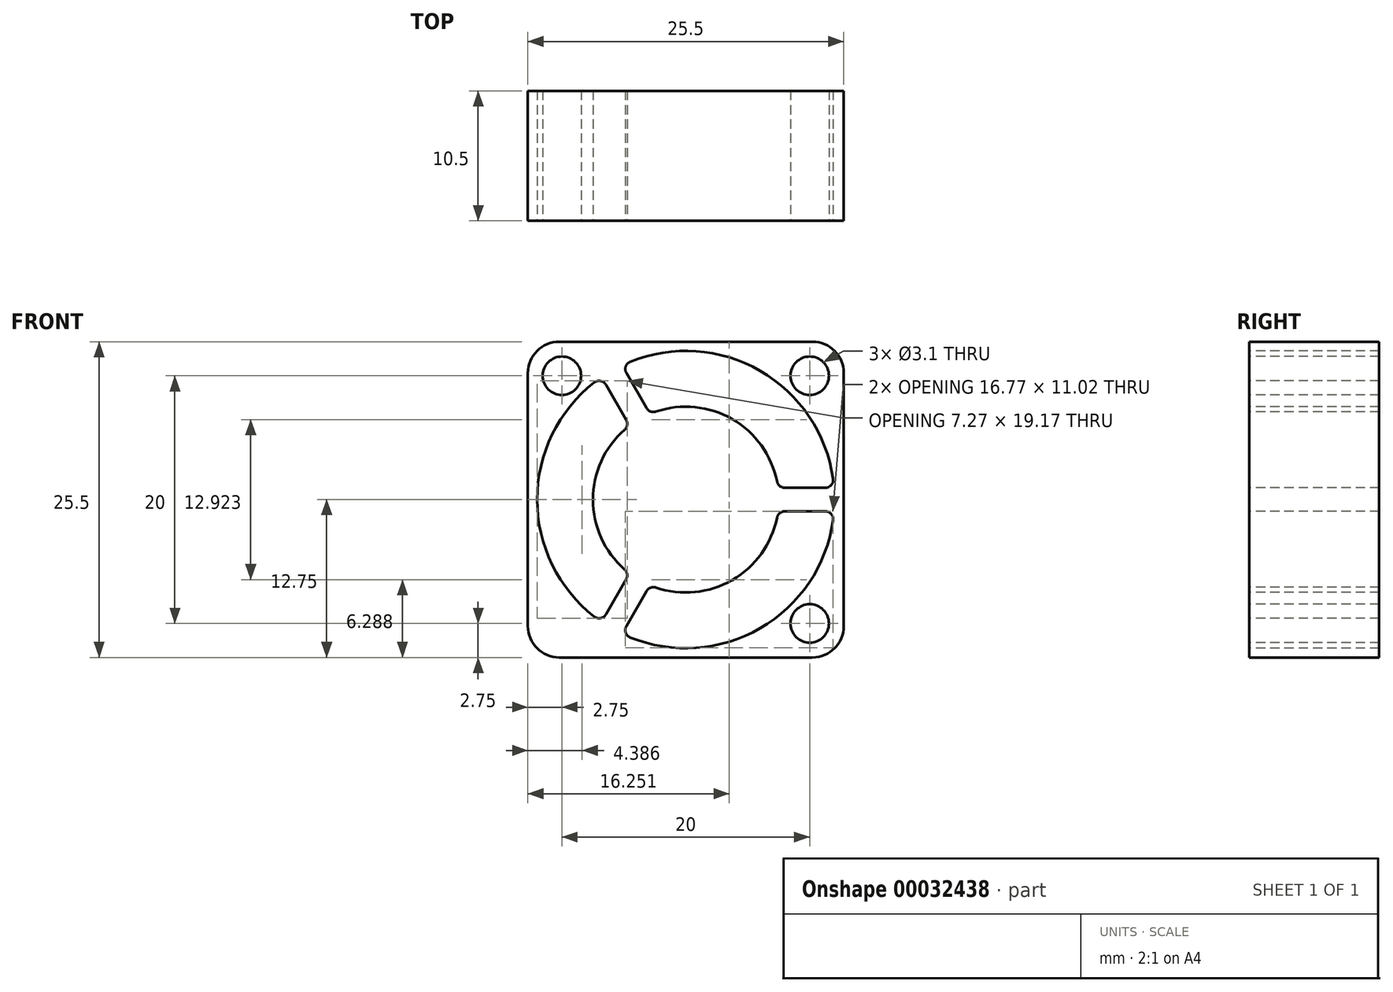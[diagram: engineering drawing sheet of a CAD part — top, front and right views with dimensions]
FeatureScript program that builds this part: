
annotation { "Feature Type Name" : "Feature", "Feature Type Description" : "" }
export const myFeature = defineFeature(function(context is Context, id is Id, definition is map)
    precondition{}
    {
        {
            var Q0;
            Q0=qCreatedBy(makeId("Front.planeOp"),FACE);
            var sketch = newSketch(context, id + "F0", { "sketchPlane" : qUnion([Q0])});
            skLineSegment(sketch, "E0.rect.bottom", {"start": v(12.75, 12.75) * mm, "end": v(-12.75, 12.75) * mm});
            skLineSegment(sketch, "E0.rect.top", {"start": v(12.75, -12.75) * mm, "end": v(-12.75, -12.75) * mm});
            skLineSegment(sketch, "E0.rect.left", {"start": v(12.75, 12.75) * mm, "end": v(12.75, -12.75) * mm});
            skLineSegment(sketch, "E0.rect.right", {"start": v(-12.75, 12.75) * mm, "end": v(-12.75, -12.75) * mm});
            skPoint(sketch, "E0.rect.middle", {"position": v(0, 0) * mm});
            skSolve(sketch);
        }
        {
            var Q0;
            Q0=makeQuery(id+"F0.imprint","IMPRINT",FACE,{"disambiguationData":[TD([[makeQuery(id+"F0.imprint","IMPRINT",EDGE,{"derivedFrom":sQuery(id+"F0.wireOp",EDGE,"E0.rect.bottom")}),1.0]])]});
            extrude(context, id + "F1", {"entities" : qUnion([Q0]), "depth" : 10.5 * mm});
        }
        {
            var Q0;
            Q0=makeQuery(id+"F1.opExtrude","SWEPT_EDGE",EDGE,{"disambiguationData":[OSD([sQuery(id+"F0.wireOp",EDGE,"E0.rect.bottom"),sQuery(id+"F0.wireOp",EDGE,"E0.rect.left")])]});
            var Q1;
            Q1=makeQuery(id+"F1.opExtrude","SWEPT_EDGE",EDGE,{"disambiguationData":[OSD([sQuery(id+"F0.wireOp",EDGE,"E0.rect.bottom"),sQuery(id+"F0.wireOp",EDGE,"E0.rect.right")])]});
            var Q2;
            Q2=makeQuery(id+"F1.opExtrude","SWEPT_EDGE",EDGE,{"disambiguationData":[OSD([sQuery(id+"F0.wireOp",EDGE,"E0.rect.top"),sQuery(id+"F0.wireOp",EDGE,"E0.rect.left")])]});
            var Q3;
            Q3=makeQuery(id+"F1.opExtrude","SWEPT_EDGE",EDGE,{"disambiguationData":[OSD([sQuery(id+"F0.wireOp",EDGE,"E0.rect.top"),sQuery(id+"F0.wireOp",EDGE,"E0.rect.right")])]});
            fillet(context, id + "F2", {"entities" : qUnion([Q0, Q1, Q2, Q3]), "radius" : 2.54 * mm, "tangentPropagation" : true, "allowEdgeOverflow" : false});
        }
        {
            var Q0;
            Q0=makeQuery(id+"F1.opExtrude","CAP_FACE",FACE,{"disambiguationData":[OSD([sQuery(id+"F0.wireOp",EDGE,"E0.rect.bottom"),sQuery(id+"F0.wireOp",EDGE,"E0.rect.top"),sQuery(id+"F0.wireOp",EDGE,"E0.rect.left"),sQuery(id+"F0.wireOp",EDGE,"E0.rect.right")])],"isStart":false});
            var sketch = newSketch(context, id + "F3", { "sketchPlane" : qUnion([Q0])});
            skCircle(sketch, "E1", {"center": v(-10, 10) * mm, "radius": 1.55 * mm});
            skCircle(sketch, "E2", {"center": v(10, 10) * mm, "radius": 1.55 * mm});
            skCircle(sketch, "E3", {"center": v(10, -10) * mm, "radius": 1.55 * mm});
            skArc(sketch, "E4", {"start": v(-4.95, 5.64) * mm, "mid": v(-7.5, 0) * mm, "end": v(-4.95, -5.64) * mm});
            skArc(sketch, "E5", {"start": v(-7.4, 9.45) * mm, "mid": v(-12, 0) * mm, "end": v(-7.4, -9.45) * mm});
            skLineSegment(sketch, "E6", {"start": v(-3.75, 6.5) * mm, "end": v(-6, 10.4) * mm, "construction": true});
            skLineSegment(sketch, "E7", {"start": v(7.5, 0) * mm, "end": v(12, 0) * mm, "construction": true});
            skLineSegment(sketch, "E8", {"start": v(-3.75, -6.5) * mm, "end": v(-6, -10.4) * mm, "construction": true});
            skLineSegment(sketch, "E9.0.left", {"start": v(-4.81, 6.43) * mm, "end": v(-6.45, 9.27) * mm});
            skLineSegment(sketch, "E9.0.right", {"start": v(-3.16, 7.39) * mm, "end": v(-4.8, 10.22) * mm});
            skLineSegment(sketch, "E10.0.left", {"start": v(7.98, 0.95) * mm, "end": v(11.25, 0.95) * mm});
            skLineSegment(sketch, "E10.0.right", {"start": v(7.98, -0.95) * mm, "end": v(11.25, -0.95) * mm});
            skLineSegment(sketch, "E10.1.left", {"start": v(-3.16, -7.39) * mm, "end": v(-4.8, -10.22) * mm});
            skLineSegment(sketch, "E10.1.right", {"start": v(-4.81, -6.43) * mm, "end": v(-6.45, -9.27) * mm});
            skLineSegment(sketch, "E11", {"start": v(-10, 10) * mm, "end": v(0, 0) * mm, "construction": true});
            skLineSegment(sketch, "E12", {"start": v(10, 10) * mm, "end": v(0, 0) * mm, "construction": true});
            skLineSegment(sketch, "E13", {"start": v(10, -10) * mm, "end": v(0, 0) * mm, "construction": true});
            skLineSegment(sketch, "E14", {"start": v(-5.68, 7.92) * mm, "end": v(-4.03, 8.88) * mm, "construction": true});
            skLineSegment(sketch, "E15", {"start": v(-5.68, -7.92) * mm, "end": v(-4.03, -8.88) * mm, "construction": true});
            skLineSegment(sketch, "E16", {"start": v(9.7, -0.95) * mm, "end": v(9.7, 0.95) * mm, "construction": true});
            skArc(sketch, "E17.trimOffspring", {"start": v(7.36, 1.46) * mm, "mid": v(3.75, 6.5) * mm, "end": v(-2.41, 7.1) * mm});
            skArc(sketch, "E18.trimOffspring", {"start": v(11.88, 1.68) * mm, "mid": v(6, 10.4) * mm, "end": v(-4.49, 11.13) * mm});
            skArc(sketch, "E19.trimOffspring", {"start": v(-2.41, -7.1) * mm, "mid": v(3.75, -6.5) * mm, "end": v(7.36, -1.46) * mm});
            skArc(sketch, "E20.trimOffspring", {"start": v(-4.49, -11.13) * mm, "mid": v(6, -10.4) * mm, "end": v(11.88, -1.68) * mm});
            skPoint(sketch, "E21.visualSharp", {"position": v(-6.8, 9.88) * mm});
            skArc(sketch, "E21.filletArc", {"start": v(-6.45, 9.27) * mm, "mid": v(-6.88, 9.58) * mm, "end": v(-7.4, 9.45) * mm});
            skPoint(sketch, "E22.visualSharp", {"position": v(-4.54, 5.97) * mm});
            skArc(sketch, "E22.filletArc", {"start": v(-4.95, 5.64) * mm, "mid": v(-4.74, 6.01) * mm, "end": v(-4.81, 6.43) * mm});
            skPoint(sketch, "E23.visualSharp", {"position": v(-2.9, 6.92) * mm});
            skArc(sketch, "E23.filletArc", {"start": v(-3.16, 7.39) * mm, "mid": v(-2.84, 7.1) * mm, "end": v(-2.41, 7.1) * mm});
            skPoint(sketch, "E24.visualSharp", {"position": v(-5.16, 10.84) * mm});
            skArc(sketch, "E24.filletArc", {"start": v(-4.49, 11.13) * mm, "mid": v(-4.85, 10.75) * mm, "end": v(-4.8, 10.22) * mm});
            skPoint(sketch, "E25.visualSharp", {"position": v(7.44, 0.95) * mm});
            skArc(sketch, "E25.filletArc", {"start": v(7.36, 1.46) * mm, "mid": v(7.58, 1.1) * mm, "end": v(7.98, 0.95) * mm});
            skPoint(sketch, "E26.visualSharp", {"position": v(11.96, 0.95) * mm});
            skArc(sketch, "E26.filletArc", {"start": v(11.25, 0.95) * mm, "mid": v(11.73, 1.17) * mm, "end": v(11.88, 1.68) * mm});
            skPoint(sketch, "E27.visualSharp", {"position": v(11.96, -0.95) * mm});
            skArc(sketch, "E27.filletArc", {"start": v(11.88, -1.68) * mm, "mid": v(11.73, -1.17) * mm, "end": v(11.25, -0.95) * mm});
            skPoint(sketch, "E28.visualSharp", {"position": v(7.44, -0.95) * mm});
            skArc(sketch, "E28.filletArc", {"start": v(7.98, -0.95) * mm, "mid": v(7.58, -1.1) * mm, "end": v(7.36, -1.46) * mm});
            skPoint(sketch, "E29.visualSharp", {"position": v(-2.9, -6.92) * mm});
            skArc(sketch, "E29.filletArc", {"start": v(-2.41, -7.1) * mm, "mid": v(-2.84, -7.1) * mm, "end": v(-3.16, -7.39) * mm});
            skPoint(sketch, "E30.visualSharp", {"position": v(-4.54, -5.97) * mm});
            skArc(sketch, "E30.filletArc", {"start": v(-4.81, -6.43) * mm, "mid": v(-4.74, -6.01) * mm, "end": v(-4.95, -5.64) * mm});
            skPoint(sketch, "E31.visualSharp", {"position": v(-6.8, -9.88) * mm});
            skArc(sketch, "E31.filletArc", {"start": v(-7.4, -9.45) * mm, "mid": v(-6.88, -9.58) * mm, "end": v(-6.45, -9.27) * mm});
            skPoint(sketch, "E32.visualSharp", {"position": v(-5.16, -10.84) * mm});
            skArc(sketch, "E32.filletArc", {"start": v(-4.8, -10.22) * mm, "mid": v(-4.85, -10.75) * mm, "end": v(-4.49, -11.13) * mm});
            skSolve(sketch);
        }
        {
            var Q0;
            Q0 = qSketchRegion(id + "F3", true);
            extrude(context, id + "F4", {"entities" : qUnion([Q0]), "operationType" : NewBodyOperationType.REMOVE, "endBound" : BoundingType.THROUGH_ALL, "oppositeDirection" : true, "depth" : 25.4 * mm});
        }
    });
